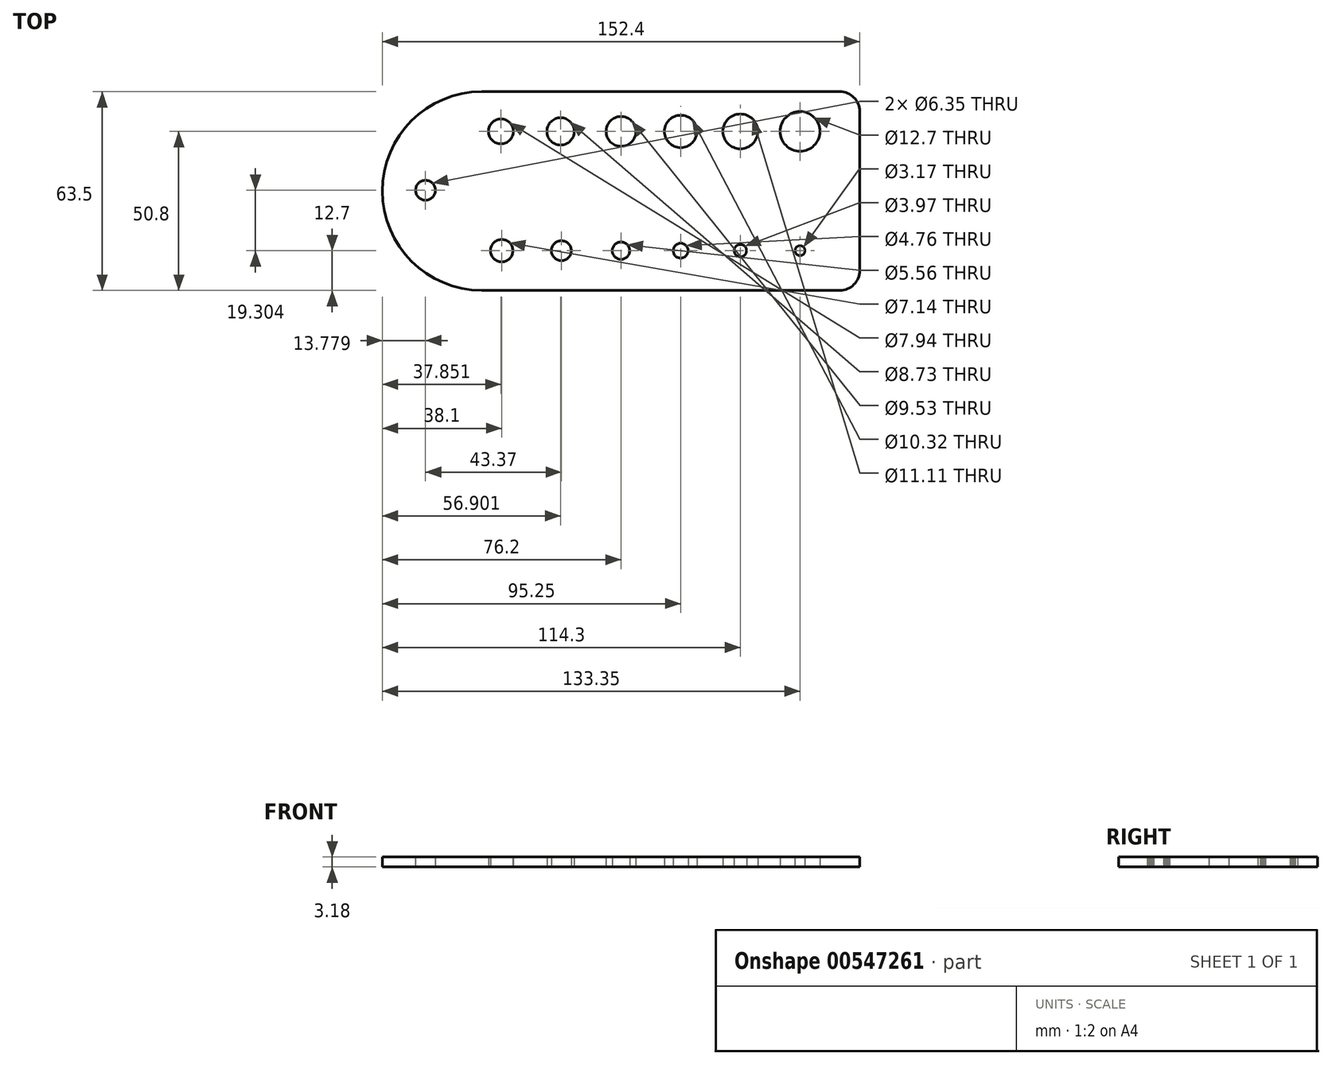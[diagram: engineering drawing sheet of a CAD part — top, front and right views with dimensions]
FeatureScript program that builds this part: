
annotation { "Feature Type Name" : "Feature", "Feature Type Description" : "" }
export const myFeature = defineFeature(function(context is Context, id is Id, definition is map)
    precondition{}
    {
        {
            var Q0;
            Q0=qCreatedBy(makeId("Top.planeOp"),FACE);
            var sketch = newSketch(context, id + "F0", { "sketchPlane" : qUnion([Q0])});
            skLineSegment(sketch, "E0.bottom", {"start": v(0, 0) * mm, "end": v(114.3, 0) * mm});
            skLineSegment(sketch, "E0.top", {"start": v(0, 63.5) * mm, "end": v(114.3, 63.5) * mm});
            skLineSegment(sketch, "E0.right", {"start": v(120.65, 6.35) * mm, "end": v(120.65, 57.15) * mm});
            skPoint(sketch, "E1.visualSharp", {"position": v(120.65, 63.5) * mm});
            skArc(sketch, "E1.filletArc", {"start": v(120.65, 57.15) * mm, "mid": v(118.8, 61.64) * mm, "end": v(114.3, 63.5) * mm});
            skPoint(sketch, "E2.visualSharp", {"position": v(120.65, 0) * mm});
            skArc(sketch, "E2.filletArc", {"start": v(114.3, 0) * mm, "mid": v(118.8, 1.86) * mm, "end": v(120.65, 6.35) * mm});
            skArc(sketch, "E3", {"start": v(0, 63.5) * mm, "mid": v(-31.75, 31.75) * mm, "end": v(0, 0) * mm});
            skCircle(sketch, "E4", {"center": v(101.6, 50.8) * mm, "radius": 6.35 * mm});
            skCircle(sketch, "E5", {"center": v(101.6, 12.7) * mm, "radius": 1.59 * mm});
            skCircle(sketch, "E6.1.0.0", {"center": v(82.55, 12.7) * mm, "radius": 1.98 * mm});
            skCircle(sketch, "E6.2.0.0", {"center": v(63.5, 12.7) * mm, "radius": 2.38 * mm});
            skCircle(sketch, "E6.3.0.0", {"center": v(44.45, 12.7) * mm, "radius": 2.78 * mm});
            skCircle(sketch, "E6.4.0.0", {"center": v(25.4, 12.7) * mm, "radius": 6553.2 * mm});
            skCircle(sketch, "E6.5.0.0", {"center": v(25.4, 12.7) * mm, "radius": 3.18 * mm});
            skLineSegment(sketch, "E6.direction1", {"start": v(101.6, 12.7) * mm, "end": v(82.55, 12.7) * mm, "construction": true});
            skCircle(sketch, "E7.1.0.0", {"center": v(82.55, 50.8) * mm, "radius": 5.56 * mm});
            skCircle(sketch, "E7.2.0.0", {"center": v(63.5, 50.8) * mm, "radius": 5.16 * mm});
            skCircle(sketch, "E7.3.0.0", {"center": v(44.45, 50.8) * mm, "radius": 4.76 * mm});
            skCircle(sketch, "E7.4.0.0", {"center": v(25.15, 50.8) * mm, "radius": 4.37 * mm});
            skLineSegment(sketch, "E7.direction1", {"start": v(101.6, 50.8) * mm, "end": v(82.55, 50.8) * mm, "construction": true});
            skCircle(sketch, "E8", {"center": v(6.1, 50.8) * mm, "radius": 3.97 * mm});
            skCircle(sketch, "E9", {"center": v(6.35, 12.7) * mm, "radius": 3.57 * mm});
            skCircle(sketch, "E10", {"center": v(-17.97, 32) * mm, "radius": 3.18 * mm});
            skSolve(sketch);
        }
        {
            var Q0;
            Q0=makeQuery(id+"F0.imprint","IMPRINT",FACE,{"disambiguationData":[TD([[makeQuery(id+"F0.imprint","IMPRINT",EDGE,{"derivedFrom":sQuery(id+"F0.wireOp",EDGE,"E0.bottom")}),1.0]])]});
            extrude(context, id + "F1", {"entities" : qUnion([Q0]), "depth" : 3.17 * mm, "offsetDistance" : 25.4 * mm});
        }
    });
